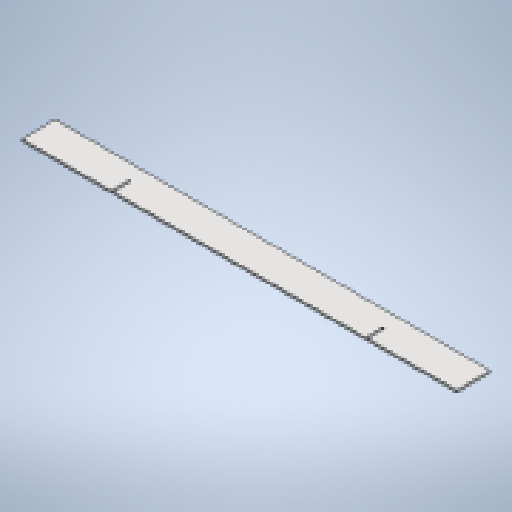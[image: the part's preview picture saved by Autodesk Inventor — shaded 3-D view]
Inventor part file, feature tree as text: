
AUTODESK INVENTOR PART (.ipt)
format: ipt  version: 2025 (Build 290162010, 162A)  size: 224,768 bytes
history: native  units: mm
features: sketch x4, extrude x2, other x2, sheet_metal_op x1, projected_geometry x1
ambient origin geometry x8: Origin, YZ Plane, XZ Plane, XY Plane, X Axis, Y Axis, Z Axis, Center Point
bodies: Body1 (feature_tree)
feature tree (10):
  sheet_metal_op  "Face1"
  extrude  "Extrusion1"  Depth=800.0mm
  extrude  "Extrusion2"  Depth=50.0mm
  other  "Mark1"
  sketch  "Sketch1"  dims[d16=50.0mm d17=800.0mm]
  other  "Plate2"
  sketch  "Sketch2"  dims[d18=50.0mm d19=50.0mm]
  sketch  "Sketch3"  dims[d20=3.0mm]
  projected_geometry  "Projected Loop1"
  sketch  "Sketch4"  dims[d21=190.0mm d22=3.0mm d23=26.0mm d24=10.0mm d25=0.0mm d26=190.0mm d27=26.0mm d28=3.0mm d29=75.0mm d30=75.0mm d31=0.0mm d32=0.0mm]
